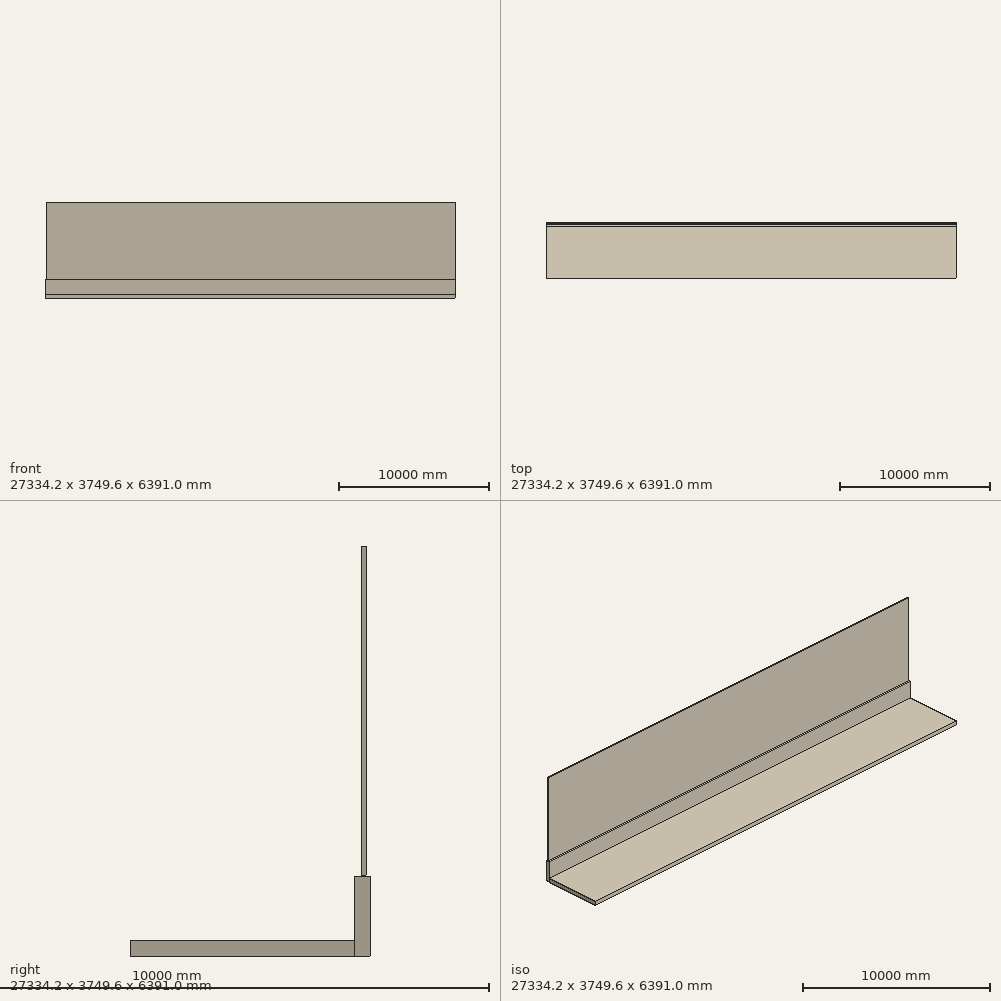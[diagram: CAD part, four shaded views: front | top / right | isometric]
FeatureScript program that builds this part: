
annotation { "Feature Type Name" : "Feature", "Feature Type Description" : "" }
export const myFeature = defineFeature(function(context is Context, id is Id, definition is map)
    precondition{}
    {
        {
            var Q0;
            Q0=qCreatedBy(makeId("Top.planeOp"),FACE);
            var sketch = newSketch(context, id + "F0", { "sketchPlane" : qUnion([Q0])});
            skLineSegment(sketch, "E0.bottom", {"start": v(-13653.67, -3086.65) * mm, "end": v(13646.33, -3086.65) * mm});
            skLineSegment(sketch, "E0.top", {"start": v(-13653.67, -6586.65) * mm, "end": v(13646.33, -6586.65) * mm});
            skLineSegment(sketch, "E0.left", {"start": v(-13653.67, -3086.65) * mm, "end": v(-13653.67, -6586.65) * mm});
            skLineSegment(sketch, "E0.right", {"start": v(13646.33, -3086.65) * mm, "end": v(13646.33, -6586.65) * mm});
            skSolve(sketch);
        }
        {
            var Q0;
            Q0=qCreatedBy(makeId("Top.planeOp"),FACE);
            var sketch = newSketch(context, id + "F1", { "sketchPlane" : qUnion([Q0])});
            skLineSegment(sketch, "E1.bottom", {"start": v(-13619.48, -3087.02) * mm, "end": v(13680.52, -3087.02) * mm});
            skLineSegment(sketch, "E1.top", {"start": v(-13619.48, -2837.02) * mm, "end": v(13680.52, -2837.02) * mm});
            skLineSegment(sketch, "E1.left", {"start": v(-13619.48, -3087.02) * mm, "end": v(-13619.48, -2837.02) * mm});
            skLineSegment(sketch, "E1.right", {"start": v(13680.52, -3087.02) * mm, "end": v(13680.52, -2837.02) * mm});
            skSolve(sketch);
        }
        {
            var Q0;
            Q0=qSketchRegion(id+"F0",true);
            extrude(context, id + "F2", {"entities" : qUnion([Q0]), "oppositeDirection" : true, "depth" : 250 * mm});
        }
        {
            var Q0;
            Q0=qSketchRegion(id+"F1",true);
            extrude(context, id + "F3", {"entities" : qUnion([Q0]), "depth" : 1000 * mm, "hasSecondDirection" : true, "secondDirectionOppositeDirection" : true, "secondDirectionDepth" : 250 * mm});
        }
        {
            var Q0;
            Q0=qCreatedBy(makeId("Front.planeOp"),FACE);
            var sketch = newSketch(context, id + "F4", { "sketchPlane" : qUnion([Q0])});
            skLineSegment(sketch, "E2.bottom", {"start": v(-13605.15, 1018.78) * mm, "end": v(13657.38, 1018.78) * mm});
            skLineSegment(sketch, "E2.top", {"start": v(-13605.15, 6141) * mm, "end": v(13657.38, 6141) * mm});
            skLineSegment(sketch, "E2.left", {"start": v(-13605.15, 1018.78) * mm, "end": v(-13605.15, 6141) * mm});
            skLineSegment(sketch, "E2.right", {"start": v(13657.38, 1018.78) * mm, "end": v(13657.38, 6141) * mm});
            skSolve(sketch);
        }
        {
            var Q0;
            Q0 = qSketchRegion(id + "F4", true);
            extrude(context, id + "F5", {"entities" : qUnion([Q0]), "depth" : 2975 * mm, "hasSecondDirection" : true, "secondDirectionOppositeDirection" : false, "secondDirectionDepth" : 2900 * mm});
        }
    });
